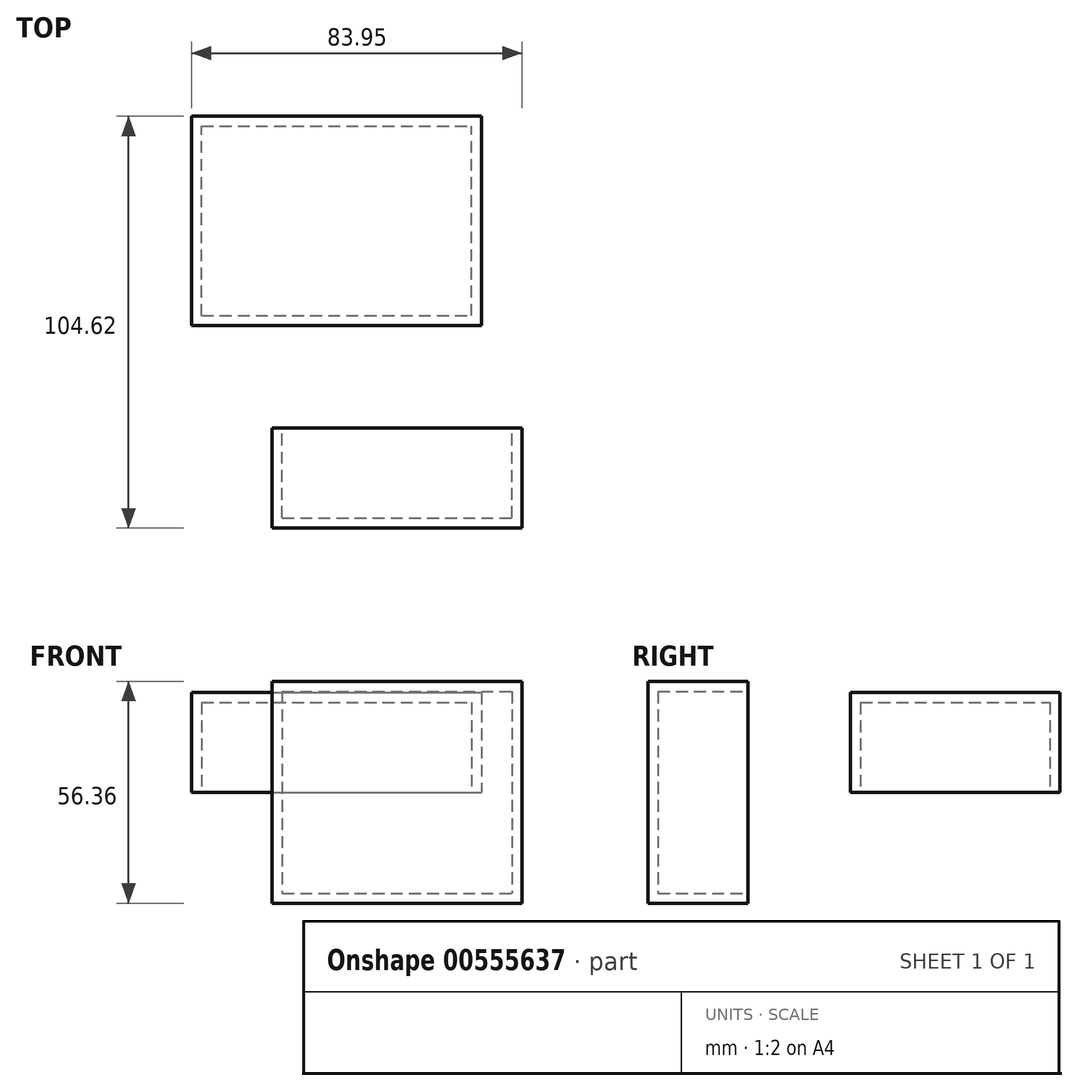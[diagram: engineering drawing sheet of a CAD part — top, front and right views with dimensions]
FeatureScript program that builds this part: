
annotation { "Feature Type Name" : "Feature", "Feature Type Description" : "" }
export const myFeature = defineFeature(function(context is Context, id is Id, definition is map)
    precondition{}
    {
        {
            var Q0;
            Q0=qCreatedBy(makeId("Front.planeOp"),FACE);
            var sketch = newSketch(context, id + "F0", { "sketchPlane" : qUnion([Q0])});
            skLineSegment(sketch, "E0.bottom", {"start": v(-31.73, 28.18) * mm, "end": v(31.73, 28.18) * mm});
            skLineSegment(sketch, "E0.top", {"start": v(-31.73, -28.18) * mm, "end": v(31.73, -28.18) * mm});
            skLineSegment(sketch, "E0.left", {"start": v(-31.73, 28.18) * mm, "end": v(-31.73, -28.18) * mm});
            skLineSegment(sketch, "E0.right", {"start": v(31.73, 28.18) * mm, "end": v(31.73, -28.18) * mm});
            skPoint(sketch, "E0.middle", {"position": v(0, 0) * mm});
            skSolve(sketch);
        }
        {
            var Q0;
            Q0=makeQuery(id+"F0.imprint","IMPRINT",FACE,{"disambiguationData":[TD([[makeQuery(id+"F0.imprint","IMPRINT",EDGE,{"derivedFrom":sQuery(id+"F0.wireOp",EDGE,"E0.bottom")}),-1.0]])]});
            extrude(context, id + "F1", {"entities" : qUnion([Q0]), "depth" : 25.4 * mm, "offsetDistance" : 25.4 * mm});
        }
        {
            var Q0;
            Q0=qCreatedBy(makeId("Top.planeOp"),FACE);
            var sketch = newSketch(context, id + "F2", { "sketchPlane" : qUnion([Q0])});
            skLineSegment(sketch, "E1.bottom", {"start": v(-52.22, 26.01) * mm, "end": v(21.48, 26.01) * mm});
            skLineSegment(sketch, "E1.top", {"start": v(-52.22, 79.22) * mm, "end": v(21.48, 79.22) * mm});
            skLineSegment(sketch, "E1.left", {"start": v(-52.22, 26.01) * mm, "end": v(-52.22, 79.22) * mm});
            skLineSegment(sketch, "E1.right", {"start": v(21.48, 26.01) * mm, "end": v(21.48, 79.22) * mm});
            skPoint(sketch, "E1.middle", {"position": v(-15.37, 52.62) * mm});
            skSolve(sketch);
        }
        {
            var Q0;
            Q0=makeQuery(id+"F2.imprint","IMPRINT",FACE,{"disambiguationData":[TD([[makeQuery(id+"F2.imprint","IMPRINT",EDGE,{"derivedFrom":sQuery(id+"F2.wireOp",EDGE,"E1.bottom")}),1.0]])]});
            extrude(context, id + "F3", {"entities" : qUnion([Q0]), "depth" : 25.4 * mm, "offsetDistance" : 25.4 * mm});
        }
        {
            var Q0;
            Q0=makeQuery(id+"F3.opExtrude","CAP_FACE",FACE,{"disambiguationData":[OSD([sQuery(id+"F2.wireOp",EDGE,"E1.bottom"),sQuery(id+"F2.wireOp",EDGE,"E1.top"),sQuery(id+"F2.wireOp",EDGE,"E1.left"),sQuery(id+"F2.wireOp",EDGE,"E1.right")])],"isStart":true});
            var Q1;
            Q1=makeQuery(id+"F1.opExtrude","CAP_FACE",FACE,{"disambiguationData":[OSD([sQuery(id+"F0.wireOp",EDGE,"E0.bottom"),sQuery(id+"F0.wireOp",EDGE,"E0.top"),sQuery(id+"F0.wireOp",EDGE,"E0.left"),sQuery(id+"F0.wireOp",EDGE,"E0.right")])],"isStart":true});
            shell(context, id + "F4", {"entities" : qUnion([Q0, Q1]), "thickness" : 2.54 * mm});
        }
    });
